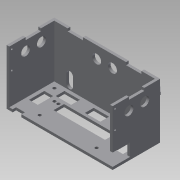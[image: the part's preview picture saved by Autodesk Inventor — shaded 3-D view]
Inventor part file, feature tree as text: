
AUTODESK INVENTOR PART (.ipt)
format: ipt  version: 2015 SP1 (Build 190203100, 203)  size: 1,003,520 bytes
history: native  units: mm
features: extrude x19, sketch x16, projected_geometry x3, fillet x1, plane x1, chamfer x1
ambient origin geometry x8: Origin, YZ Plane, XZ Plane, XY Plane, X Axis, Y Axis, Z Axis, Center Point
bodies: Body1 (feature_tree)
feature tree (41):
  sketch  "Sketch1"  dims[d49=120.812mm d51=3.0mm]
  extrude  "Extrusion5"  Depth=3.0mm
  extrude  "Extrusion6"  Depth=60.0mm TaperAngle=0.0deg
  extrude  "Extrusion7"  Depth=3.0mm
  extrude  "Extrusion8"  Depth=51.214111mm
  extrude  "Extrusion9"  Depth=10.0mm TaperAngle=0.0deg
  extrude  "Extrusion10"  Depth=17.5mm
  sketch  "Sketch12"  dims[d65=10.0mm d66=17.5mm]
  extrude  "Extrusion11"  Depth=10.0mm TaperAngle=0.0deg
  extrude  "Extrusion12"  Depth=10.0mm TaperAngle=0.0deg
  fillet  "Fillet2"  Radius=22.0mm
  extrude  "Extrusion13"  Depth=15.0mm
  plane  "Work Plane1"
  sketch  "Sketch20"  dims[d80=3.0mm d81=0.0mm d82=10.0mm d83=0.0mm d84=22.0mm]
  extrude  "Extrusion26"  Depth=200.0mm TaperAngle=0.0deg
  sketch  "Sketch25"  dims[d87=10.0mm d88=200.0mm d89=0.0mm]
  extrude  "Extrusion28"  Depth=2.0mm
  extrude  "Extrusion29"  Depth=3.5mm
  extrude  "Extrusion30"  Depth=20.0mm
  chamfer  "Chamfer1"  Distance=10.0mm
  extrude  "Extrusion31"  Depth=6.5mm
  extrude  "Extrusion32"  Depth=20.0mm
  extrude  "Extrusion33"  Depth=10.0mm TaperAngle=0.0deg
  extrude  "Extrusion34"  TaperAngle=180.0deg  [1 undecoded]
  extrude  "Extrusion35"  Depth=7.5mm
  extrude  "Extrusion36"  Depth=7.5mm
  sketch  "Sketch6"  dims[d52=3.0mm d53=0.0mm d54=60.0mm d55=0.0mm]
  sketch  "Sketch7"  dims[d57=3.0mm d58=3.0mm]
  sketch  "Sketch9"  dims[d59=114.812mm d61=51.214111mm]
  sketch  "Sketch10"  dims[d62=3.5mm d63=10.0mm d64=0.0mm]
  sketch  "Sketch13"  dims[d69=10.0mm d72=10.0mm d73=0.0mm]
  sketch  "Sketch24"  dims[d85=22.0mm d86=15.0mm]
  sketch  "Sketch26"  dims[d90=200.0mm d91=0.0mm d92=2.0mm]
  sketch  "Sketch27"  dims[d95=3.5mm d96=3.5mm]
  projected_geometry  "Projected Loop1"
  projected_geometry  "Projected Loop2"
  sketch  "Sketch30"  dims[d97=3.5mm d99=20.0mm]
  sketch  "Sketch34"  dims[d100=55.0mm]
  projected_geometry  "Projected Loop6"
  sketch  "Sketch35"  dims[d101=3.5mm d102=10.0mm d103=0.0mm]
  sketch  "Sketch38"  dims[d121=19.75mm d132=6.5mm d164=20.0mm d165=10.0mm d166=0.0mm d167=180.0deg d168=7.5mm d169=7.5mm d172=22.5mm d173=3.0mm d174=22.5mm d175=15.0mm d176=0.0mm d177=7.5mm d178=7.5mm d179=15.0mm d180=0.0mm d187=2.0mm d188=3.0mm d189=6.5mm d190=2.0mm d191=3.0mm d192=6.5mm d193=2.0mm d194=3.0mm d195=2.0mm d196=3.0mm d197=6.5mm d198=6.5mm d199=0.5mm d200=15.0mm d201=0.0mm d202=5.0mm d203=2.0mm d204=45.0deg d223=10.0mm d224=0.0mm d225=17.5mm d226=10.0mm d227=17.5mm d228=6.0mm d229=10.0mm d230=0.0mm d240=10.25mm d241=10.25mm d242=18.0mm d243=9.0mm d246=10.25mm d247=10.25mm d248=18.0mm d249=9.0mm d250=10.0mm d251=0.0mm d252=10.0mm d253=0.0mm d254=37.5mm d255=37.5mm d256=79.49mm d257=7.5mm d258=7.5mm d259=5.0mm d260=5.0mm d261=10.0mm d262=0.0mm d263=2.0mm d264=0.0mm]
note: 1 required parameter value undecoded (feature->parameter linkage not recoverable at this tier; creation-order binding heuristic only, values carry confidence <= 0.55)
